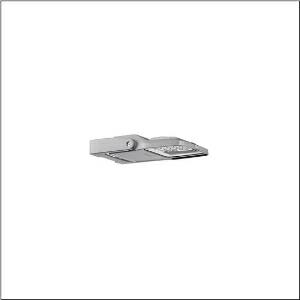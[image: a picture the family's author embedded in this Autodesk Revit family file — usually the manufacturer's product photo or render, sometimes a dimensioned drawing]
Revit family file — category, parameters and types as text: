
# Revit family: floodlight_fl_21_micro___pl64_5xa7762a4e2a_3ce2
name_source: partatom
category: Lighting Fixtures
units: mm (PartAtom-declared; Revit-internal decimal feet)

## family parameters
Cut with Voids When Loaded = No
Host = Face
Light Source = No
Part Type = Normal
Room Calculation Point = No
Round Connector Dimension = Use Diameter
Shared = No

## types (1)
- --- (1 x LED, 2980 lm, 23.1 W, 4000K)
    Apparent Load = 23 VA
    CIE Flux Codes = 28 80 98 100 100
    Color Rendering = 70
    Color Temperature = 4000K
    Default Elevation = 1800 mm
    Description = Floodlight FL 21 micro, floodlight, primary light control with lens, of PMMA, primary optical cover: protective disc, of toughened safety glass, transparent, light distribution: PL64, light emission: direct distribution, installation type: surface-mounted, LED, High Power LED, rated luminous flux: 2.980lm, luminous efficacy: 129lm/W, light colour: 740, colour temperature: 4000K, control gear: ECG iQ, control: Auto-Match, Temp-Guard, Night-Set, Smart-Wire, Desk-Remote (wireless, voltage-free reading and setting of iQ features in the workshop via application-optimized NFC function/RFID function), optimised constant luminous flux control (CLO 2.0), Street-Remote, with terminal, 6-pole, mains connection: 220..240V, AC, 50/60Hz, start of lifetime: 23W, end of lifetime: 24W, reduction: 11W, luminaire housing, of diecast aluminium, powder-coated, Siteco® metallic grey (DB 702S), corrosivity category C5 according to DIN EN ISO 12944, design bracket, of diecast aluminium, powder-coated, Siteco® metallic grey (DB 702S), protection rating (complete): IP66, insulation class (complete): insulation class II (safety insulation), certification: CE, protection symbol: D, impact resistance: IK07, permissible operating ambient temperature: -40..+40°C, permissible operating ambient temperature for outdoor applications: -40..+50°C, standard: DIN EN 12944, packaging unit: 1 piece

Light Distribution: PL64
    Height = 65 mm
    Lamp = 1 x LED
    Lamp Light Flux = 2980 lm
    Lamp Power = 23.1 W
    Lamp count = 1
    Length = 312 mm
    Luminous efficacy = 129 lm/W
    Manufacturer = Siteco
    ModVariant = No
    Model = 5XA7762A4E2A
    Number of Poles = 1
    OnlyDefault = Yes
    Power Factor = 1
    Product Name = Floodlight FL 21 micro | PL64
    Product group = floodlight | pylon top
    ProductGroupID = 6101
    Protection Class = Protection class II
    Protection Degree = IP 66
    RLX_Detail_Level = 1
    RlxData = <blob elided: 97425 chars, md5=5c8b14b2>
    Socket = socket
    Standby Power = 0 W
    System Light Flux = 2980 lm
    System Power = 23 W
    Type Comments = factory setting: luminous flux: 100 % | dim-lin: 254 | 455 mA
    Type Image = l_1006878.jpg
    URL = http://relux.com
    VarID = @adj_094095
    Voltage = 0 V
    Weight = 0.00 kg
    Width = 230 mm

## geometry (parser evidence)
native form markers: Blend x4, Sweep x13
no freeform markers — native parametric forms only
